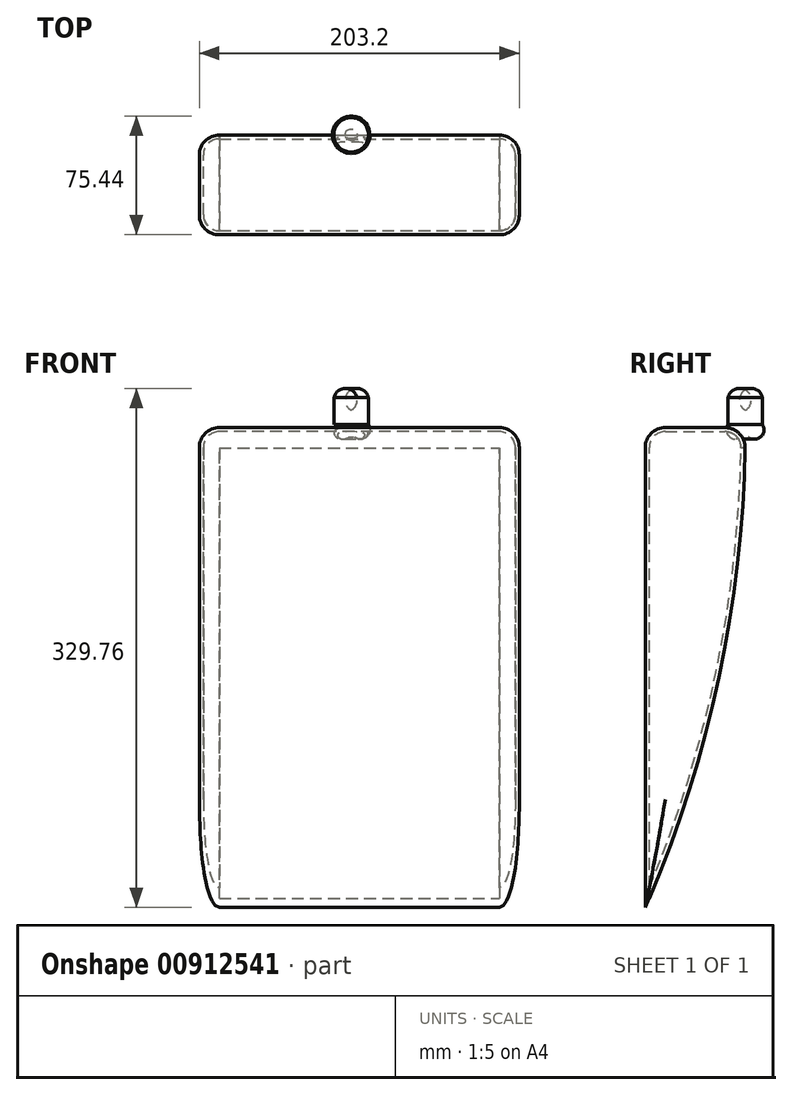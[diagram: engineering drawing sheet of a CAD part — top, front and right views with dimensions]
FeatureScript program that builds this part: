
annotation { "Feature Type Name" : "Feature", "Feature Type Description" : "" }
export const myFeature = defineFeature(function(context is Context, id is Id, definition is map)
    precondition{}
    {
        {
            var Q0;
            Q0=qCreatedBy(makeId("Front.planeOp"),FACE);
            var sketch = newSketch(context, id + "F0", { "sketchPlane" : qUnion([Q0])});
            skLineSegment(sketch, "E0", {"start": v(-49.68, 82.44) * mm, "end": v(-49.68, -222.36) * mm});
            skLineSegment(sketch, "E1", {"start": v(-49.68, -222.36) * mm, "end": v(153.52, -222.36) * mm});
            skLineSegment(sketch, "E2", {"start": v(153.52, -222.36) * mm, "end": v(153.52, 82.44) * mm});
            skLineSegment(sketch, "E3", {"start": v(153.52, 82.44) * mm, "end": v(-49.68, 82.44) * mm});
            skSolve(sketch);
        }
        {
            var Q0;
            Q0 = qSketchRegion(id + "F0", true);
            extrude(context, id + "F1", {"entities" : qUnion([Q0]), "depth" : 63.5 * mm, "offsetDistance" : 25.4 * mm});
        }
        {
            var Q0;
            Q0=makeQuery(id+"F1.opExtrude","SWEPT_FACE",FACE,{"disambiguationData":[OSD([sQuery(id+"F0.wireOp",EDGE,"E2")])]});
            var sketch = newSketch(context, id + "F2", { "sketchPlane" : qUnion([Q0])});
            skArc(sketch, "E4", {"start": v(-63.5, -222.36) * mm, "mid": v(-16.04, -73.23) * mm, "end": v(0, 82.44) * mm});
            skLineSegment(sketch, "E5", {"start": v(-63.5, -222.36) * mm, "end": v(-63.5, -259.12) * mm});
            skLineSegment(sketch, "E6", {"start": v(-63.5, -259.12) * mm, "end": v(30.33, -259.12) * mm});
            skLineSegment(sketch, "E7", {"start": v(30.33, -259.12) * mm, "end": v(30.33, 82.44) * mm});
            skLineSegment(sketch, "E8", {"start": v(30.33, 82.44) * mm, "end": v(0, 82.44) * mm});
            skSolve(sketch);
        }
        {
            var Q0;
            Q0 = qSketchRegion(id + "F2", true);
            extrude(context, id + "F3", {"entities" : qUnion([Q0]), "operationType" : NewBodyOperationType.REMOVE, "oppositeDirection" : true, "depth" : 525.02 * mm, "offsetDistance" : 25.4 * mm});
        }
        {
            var Q0;
            Q0=makeQuery(id+"F1.opExtrude","SWEPT_FACE",FACE,{"disambiguationData":[OSD([sQuery(id+"F0.wireOp",EDGE,"E0")])]});
            fillet(context, id + "F4", {"entities" : qUnion([Q0]), "radius" : 12.7 * mm, "tangentPropagation" : true, "allowEdgeOverflow" : false});
        }
        {
            var Q0;
            Q0=makeQuery(id+"F1.opExtrude","SWEPT_FACE",FACE,{"disambiguationData":[OSD([sQuery(id+"F0.wireOp",EDGE,"E2")])]});
            fillet(context, id + "F5", {"entities" : qUnion([Q0]), "radius" : 12.7 * mm, "tangentPropagation" : true, "allowEdgeOverflow" : false});
        }
        {
            var Q0;
            Q0=makeQuery(id+"F1.opExtrude","SWEPT_FACE",FACE,{"disambiguationData":[OSD([sQuery(id+"F0.wireOp",EDGE,"E3")])]});
            fillet(context, id + "F6", {"entities" : qUnion([Q0]), "radius" : 12.7 * mm, "tangentPropagation" : true, "allowEdgeOverflow" : false});
        }
        {
            var Q0;
            Q0=makeQuery(id+"F3.boolean.opBoolean","COPY",FACE,{"derivedFrom":makeQuery(id+"F3.opExtrude","SWEPT_FACE",FACE,{"disambiguationData":[OSD([sQuery(id+"F2.wireOp",EDGE,"E4")])]})});
            shell(context, id + "F7", {"entities" : qUnion([Q0]), "thickness" : 2.54 * mm});
        }
        {
            var Q0;
            Q0=qCreatedBy(makeId("Front.planeOp"),FACE);
            var sketch = newSketch(context, id + "F8", { "sketchPlane" : qUnion([Q0])});
            skLineSegment(sketch, "E9", {"start": v(46.72, 81.05) * mm, "end": v(46.72, 106.45) * mm});
            skArc(sketch, "E10", {"start": v(46.72, 106.45) * mm, "mid": v(39.96, 106.72) * mm, "end": v(35.76, 101.42) * mm});
            skLineSegment(sketch, "E11", {"start": v(35.76, 101.42) * mm, "end": v(35.76, 84.32) * mm});
            skArc(sketch, "E12", {"start": v(35.76, 84.32) * mm, "mid": v(40.02, 78.6) * mm, "end": v(46.72, 81.05) * mm});
            skArc(sketch, "E13", {"start": v(35.76, 84.32) * mm, "mid": v(39.05, 75.33) * mm, "end": v(46.72, 81.05) * mm});
            skSolve(sketch);
        }
        {
            var Q0;
            Q0 = qSketchRegion(id + "F8", true);
            var Q1;
            Q1=sQuery(id+"F8.wireOp",EDGE,"E9");
            revolve(context, id + "F9", {"operationType" : NewBodyOperationType.ADD, "surfaceOperationType" : NewSurfaceOperationType.NEW, "entities" : qUnion([Q0]), "axis" : qUnion([Q1]), "revolveType" : RevolveType.FULL});
        }
    });
